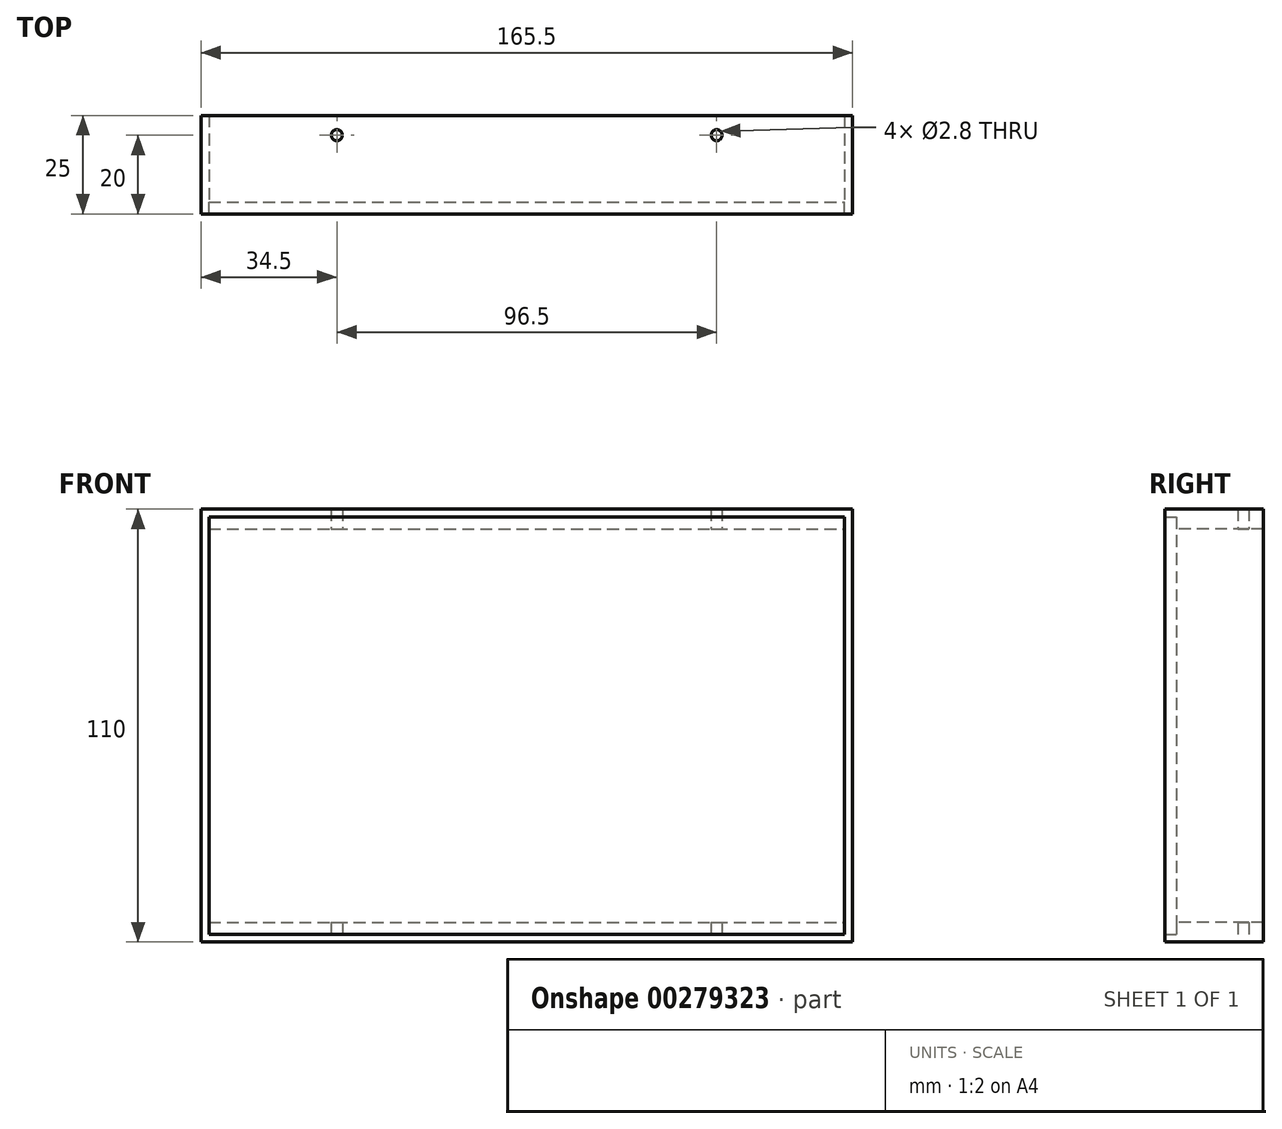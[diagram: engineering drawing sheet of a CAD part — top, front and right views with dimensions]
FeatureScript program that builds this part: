
annotation { "Feature Type Name" : "Feature", "Feature Type Description" : "" }
export const myFeature = defineFeature(function(context is Context, id is Id, definition is map)
    precondition{}
    {
        {
            var Q0;
            Q0=qCreatedBy(makeId("Front.planeOp"),FACE);
            var sketch = newSketch(context, id + "F0", { "sketchPlane" : qUnion([Q0])});
            skLineSegment(sketch, "E0.bottom", {"start": v(75.25, -46.75) * mm, "end": v(-75.25, -46.75) * mm});
            skLineSegment(sketch, "E0.top", {"start": v(75.25, 46.75) * mm, "end": v(-75.25, 46.75) * mm});
            skLineSegment(sketch, "E0.left", {"start": v(75.25, -46.75) * mm, "end": v(75.25, 46.75) * mm});
            skLineSegment(sketch, "E0.right", {"start": v(-75.25, -46.75) * mm, "end": v(-75.25, 46.75) * mm});
            skPoint(sketch, "E0.middle", {"position": v(0, 0) * mm});
            skLineSegment(sketch, "E1.bottom", {"start": v(-81.75, 50.75) * mm, "end": v(79.75, 50.75) * mm});
            skLineSegment(sketch, "E1.top", {"start": v(-81.75, -55.25) * mm, "end": v(79.75, -55.25) * mm});
            skLineSegment(sketch, "E1.left", {"start": v(-81.75, 50.75) * mm, "end": v(-81.75, -55.25) * mm});
            skLineSegment(sketch, "E1.right", {"start": v(79.75, 50.75) * mm, "end": v(79.75, -55.25) * mm});
            skSolve(sketch);
        }
        {
            var Q0;
            Q0=qCreatedBy(makeId("Front.planeOp"),FACE);
            var sketch = newSketch(context, id + "F1", { "sketchPlane" : qUnion([Q0])});
            skLineSegment(sketch, "E2.bottom", {"start": v(-81.75, 50.75) * mm, "end": v(79.75, 50.75) * mm});
            skLineSegment(sketch, "E2.top", {"start": v(-81.75, -55.25) * mm, "end": v(79.75, -55.25) * mm});
            skLineSegment(sketch, "E2.left", {"start": v(-81.75, 50.75) * mm, "end": v(-81.75, -55.25) * mm});
            skLineSegment(sketch, "E2.right", {"start": v(79.75, 50.75) * mm, "end": v(79.75, -55.25) * mm});
            skLineSegment(sketch, "E3.bottom", {"start": v(-83.75, 52.75) * mm, "end": v(81.75, 52.75) * mm});
            skLineSegment(sketch, "E3.top", {"start": v(-83.75, -57.25) * mm, "end": v(81.75, -57.25) * mm});
            skLineSegment(sketch, "E3.left", {"start": v(-83.75, 52.75) * mm, "end": v(-83.75, -57.25) * mm});
            skLineSegment(sketch, "E3.right", {"start": v(81.75, 52.75) * mm, "end": v(81.75, -57.25) * mm});
            skSolve(sketch);
        }
        {
            var Q0;
            Q0 = qSketchRegion(id + "F1", true);
            extrude(context, id + "F2", {"entities" : qUnion([Q0]), "depth" : 3 * mm});
        }
        {
            var Q0;
            Q0=qCreatedBy(makeId("Front.planeOp"),FACE);
            var sketch = newSketch(context, id + "F3", { "sketchPlane" : qUnion([Q0])});
            skLineSegment(sketch, "E4.bottom", {"start": v(-83.75, 52.75) * mm, "end": v(81.75, 52.75) * mm});
            skLineSegment(sketch, "E4.top", {"start": v(-83.75, -57.25) * mm, "end": v(81.75, -57.25) * mm});
            skLineSegment(sketch, "E4.left", {"start": v(-83.75, 52.75) * mm, "end": v(-83.75, -57.25) * mm});
            skLineSegment(sketch, "E4.right", {"start": v(81.75, 52.75) * mm, "end": v(81.75, -57.25) * mm});
            skLineSegment(sketch, "E5.bottom", {"start": v(-81.75, 47.75) * mm, "end": v(79.75, 47.75) * mm});
            skLineSegment(sketch, "E5.top", {"start": v(-81.75, -52.25) * mm, "end": v(79.75, -52.25) * mm});
            skLineSegment(sketch, "E5.left", {"start": v(-81.75, 47.75) * mm, "end": v(-81.75, -52.25) * mm});
            skLineSegment(sketch, "E5.right", {"start": v(79.75, 47.75) * mm, "end": v(79.75, -52.25) * mm});
            skSolve(sketch);
        }
        {
            var Q0;
            Q0 = qSketchRegion(id + "F3", true);
            extrude(context, id + "F4", {"entities" : qUnion([Q0]), "operationType" : NewBodyOperationType.ADD, "oppositeDirection" : true, "depth" : 22 * mm});
        }
        {
            var Q0;
            Q0=makeQuery(id+"F4.boolean.opBoolean","MERGE",FACE,{"derivedFrom":[makeQuery(id+"F2.opExtrude","SWEPT_FACE",FACE,{"disambiguationData":[OSD([sQuery(id+"F1.wireOp",EDGE,"E3.top")])]}),makeQuery(id+"F4.opExtrude","SWEPT_FACE",FACE,{"disambiguationData":[OSD([sQuery(id+"F3.wireOp",EDGE,"E4.top")])]})]});
            var sketch = newSketch(context, id + "F5", { "sketchPlane" : qUnion([Q0])});
            skCircle(sketch, "E6", {"center": v(-49.25, -17) * mm, "radius": 1.4 * mm});
            skCircle(sketch, "E7", {"center": v(47.25, -17) * mm, "radius": 1.4 * mm});
            skSolve(sketch);
        }
        {
            var Q0;
            Q0 = qSketchRegion(id + "F5", true);
            extrude(context, id + "F6", {"entities" : qUnion([Q0]), "operationType" : NewBodyOperationType.REMOVE, "endBound" : BoundingType.THROUGH_ALL, "oppositeDirection" : true, "depth" : 25 * mm});
        }
        {
            var Q0;
            Q0=qCreatedBy(makeId("Front.planeOp"),FACE);
            var sketch = newSketch(context, id + "F7", { "sketchPlane" : qUnion([Q0])});
            skLineSegment(sketch, "E8.bottom", {"start": v(-81.75, 50.75) * mm, "end": v(79.75, 50.75) * mm});
            skLineSegment(sketch, "E8.top", {"start": v(-81.75, -55.25) * mm, "end": v(79.75, -55.25) * mm});
            skLineSegment(sketch, "E8.left", {"start": v(-81.75, 50.75) * mm, "end": v(-81.75, -55.25) * mm});
            skLineSegment(sketch, "E8.right", {"start": v(79.75, 50.75) * mm, "end": v(79.75, -55.25) * mm});
            skSolve(sketch);
        }
        {
            var Q0;
            Q0 = qSketchRegion(id + "F7", true);
            extrude(context, id + "F8", {"entities" : qUnion([Q0]), "depth" : 3 * mm});
        }
    });
